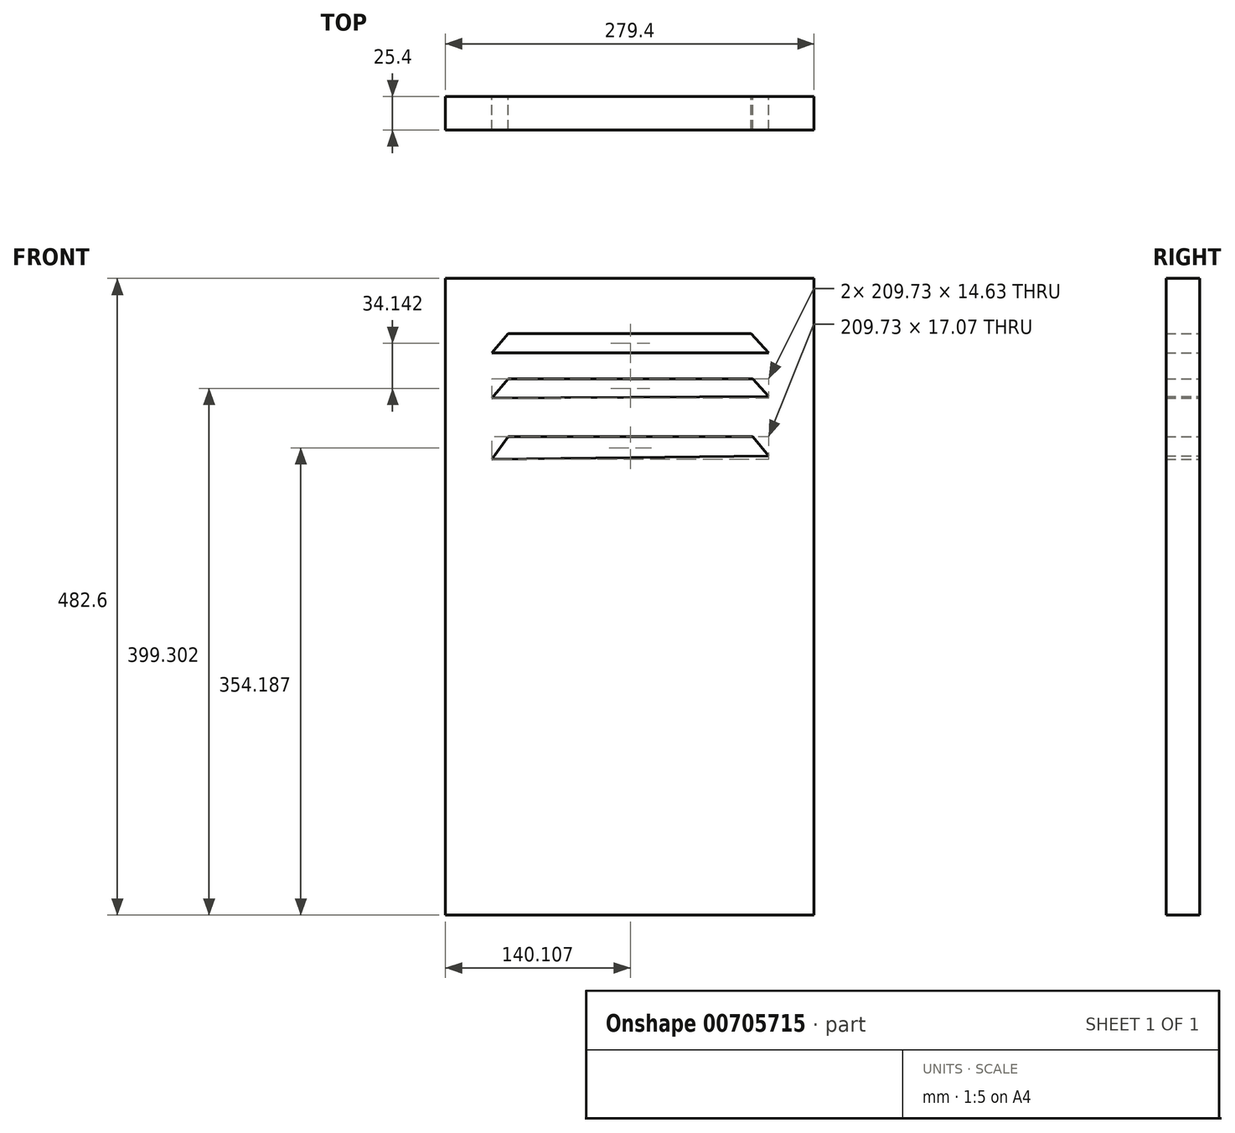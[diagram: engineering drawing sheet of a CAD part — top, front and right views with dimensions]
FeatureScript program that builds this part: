
annotation { "Feature Type Name" : "Feature", "Feature Type Description" : "" }
export const myFeature = defineFeature(function(context is Context, id is Id, definition is map)
    precondition{}
    {
        {
            var Q0;
            Q0=qCreatedBy(makeId("Front.planeOp"),FACE);
            var sketch = newSketch(context, id + "F0", { "sketchPlane" : qUnion([Q0])});
            skLineSegment(sketch, "E0.bottom", {"start": v(132.17, -52.24) * mm, "end": v(-147.23, -52.24) * mm});
            skLineSegment(sketch, "E0.top", {"start": v(132.17, 430.36) * mm, "end": v(-147.23, 430.36) * mm});
            skLineSegment(sketch, "E0.left", {"start": v(132.17, -52.24) * mm, "end": v(132.17, 430.36) * mm});
            skLineSegment(sketch, "E0.right", {"start": v(-147.23, -52.24) * mm, "end": v(-147.23, 430.36) * mm});
            skPoint(sketch, "E0.middle", {"position": v(-7.53, 189.06) * mm});
            skLineSegment(sketch, "E1", {"start": v(-99.8, 388.52) * mm, "end": v(84.33, 388.52) * mm});
            skLineSegment(sketch, "E2", {"start": v(84.33, 388.52) * mm, "end": v(97.74, 373.89) * mm});
            skLineSegment(sketch, "E3", {"start": v(97.74, 373.89) * mm, "end": v(-111.99, 373.89) * mm});
            skLineSegment(sketch, "E4", {"start": v(-111.99, 373.89) * mm, "end": v(-99.8, 388.52) * mm});
            skLineSegment(sketch, "E5", {"start": v(97.74, 340.97) * mm, "end": v(85.55, 354.38) * mm});
            skLineSegment(sketch, "E6", {"start": v(85.55, 354.38) * mm, "end": v(-99.8, 354.38) * mm});
            skLineSegment(sketch, "E7", {"start": v(-99.8, 354.38) * mm, "end": v(-111.99, 339.75) * mm});
            skLineSegment(sketch, "E8", {"start": v(-111.99, 339.75) * mm, "end": v(97.74, 340.97) * mm});
            skLineSegment(sketch, "E9", {"start": v(97.74, 295.85) * mm, "end": v(85.55, 310.48) * mm});
            skLineSegment(sketch, "E10", {"start": v(85.55, 310.48) * mm, "end": v(-99.8, 310.48) * mm});
            skLineSegment(sketch, "E11", {"start": v(-99.8, 310.48) * mm, "end": v(-111.99, 293.41) * mm});
            skLineSegment(sketch, "E12", {"start": v(-111.99, 293.41) * mm, "end": v(97.74, 295.85) * mm});
            skSolve(sketch);
        }
        {
            var Q0;
            Q0=makeQuery(id+"F0.imprint","IMPRINT",FACE,{"disambiguationData":[TD([[makeQuery(id+"F0.imprint","IMPRINT",EDGE,{"derivedFrom":sQuery(id+"F0.wireOp",EDGE,"E0.bottom")}),-1.0]])]});
            extrude(context, id + "F1", {"entities" : qUnion([Q0]), "depth" : 25.4 * mm, "offsetDistance" : 25.4 * mm});
        }
    });
